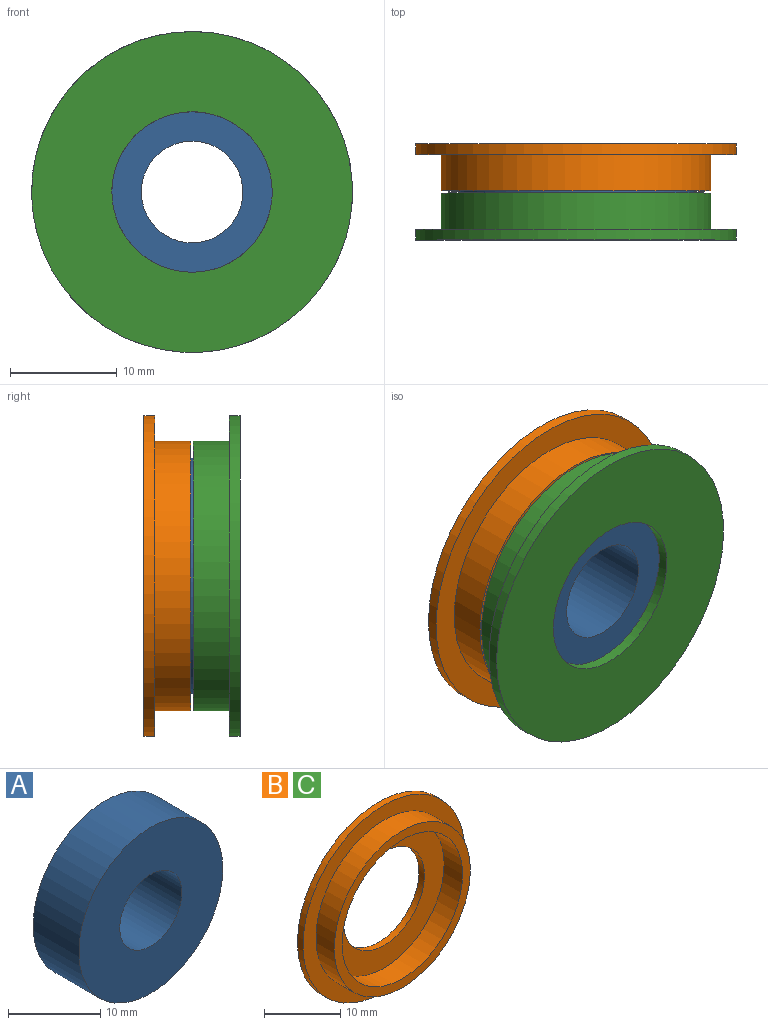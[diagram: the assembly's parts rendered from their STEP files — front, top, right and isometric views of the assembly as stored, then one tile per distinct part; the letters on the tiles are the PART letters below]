
ASSEMBLY  parts=3 mates=2
PART A: 4 faces, bbox 22x7x22 mm
  f0: cylinder r=4.75mm len=9.5mm, axis (0,1,0), area 208.9mm2, adj f2,f3
  f1: cylinder r=11mm len=22mm, axis (0,1,0), area 483.8mm2, adj f2,f3
  f2: plane 22x22mm, normal (0,-1,0), area 309.3mm2, adj f0,f1
  f3: plane 22x22mm, normal (0,1,0), area 309.3mm2, adj f0,f1
PART B: 8 faces, bbox 30x4.4x30 mm
  f0: cylinder r=7.5mm len=15mm, axis (0,1,0), area 47.1mm2, adj f5,f7
  f1: cylinder r=11.15mm len=22.3mm, axis (0,1,0), area 238.2mm2, adj f6,f7
  f2: cylinder r=12.6mm len=25.2mm, axis (0,1,0), area 269.2mm2, adj f4,f6
  f3: cylinder r=15mm len=30mm, axis (0,1,0), area 94.2mm2, adj f4,f5
  f4: plane 30x30mm, normal (0,-1,0), area 208.1mm2, adj f2,f3
  f5: plane 30x30mm, normal (0,1,0), area 530.1mm2, adj f0,f3
  f6: plane 25.2x25.2mm, normal (0,-1,0), area 108.2mm2, adj f1,f2
  f7: plane 22.3x22.3mm, normal (0,-1,0), area 213.9mm2, adj f0,f1
PART C: same geometry as B
PLACE A rot(axis=(0,-1,0),6.6deg) t=(4.15,-31.77,12.73)mm
PLACE B rot(axis=(0,1,0),173.4deg) t=(4.15,-30.77,12.73)mm
PLACE C rot(axis=(-0.67,0,-0.75),180deg) t=(4.15,-39.77,12.73)mm
MATE fastened A.f0 <-> B.f0  axis (0,1,0) through (4.15,-31.77,12.73)mm
MATE fastened A.f0 <-> C.f0  axis (0,-1,0) through (4.15,-38.77,12.73)mm
